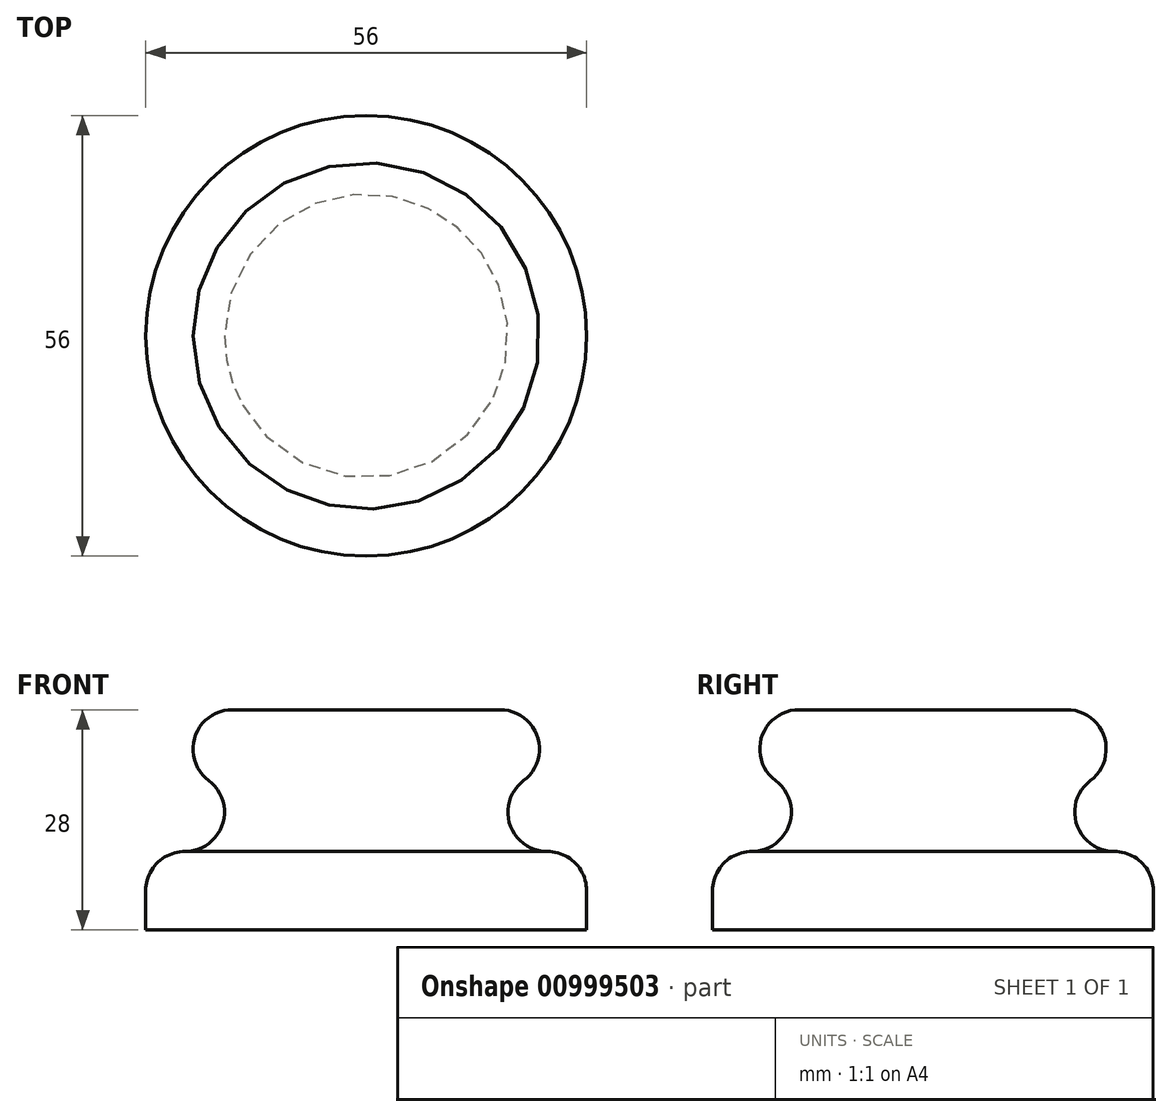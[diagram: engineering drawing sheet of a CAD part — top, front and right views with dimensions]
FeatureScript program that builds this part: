
annotation { "Feature Type Name" : "Feature", "Feature Type Description" : "" }
export const myFeature = defineFeature(function(context is Context, id is Id, definition is map)
    precondition{}
    {
        {
            var Q0;
            Q0=qCreatedBy(makeId("Front.planeOp"),FACE);
            var sketch = newSketch(context, id + "F0", { "sketchPlane" : qUnion([Q0])});
            skLineSegment(sketch, "E0", {"start": v(0, 0) * mm, "end": v(0, 28) * mm});
            skLineSegment(sketch, "E1", {"start": v(0, 0) * mm, "end": v(28, 0) * mm});
            skLineSegment(sketch, "E2", {"start": v(28, 0) * mm, "end": v(28, 5) * mm});
            skLineSegment(sketch, "E3", {"start": v(17, 28) * mm, "end": v(0, 28) * mm});
            skArc(sketch, "E4.filletArc", {"start": v(20, 19) * mm, "mid": v(21.74, 24.58) * mm, "end": v(17, 28) * mm});
            skArc(sketch, "E5.filletArc", {"start": v(20, 19) * mm, "mid": v(18.26, 13.42) * mm, "end": v(23, 10) * mm});
            skArc(sketch, "E6.filletArc", {"start": v(28, 5) * mm, "mid": v(26.54, 8.54) * mm, "end": v(23, 10) * mm});
            skLineSegment(sketch, "E7", {"start": v(7.48, 10) * mm, "end": v(42.98, 10) * mm, "construction": true});
            skSolve(sketch);
        }
        {
            var Q0;
            Q0 = qSketchRegion(id + "F0", true);
            var Q1;
            Q1=sQuery(id+"F0.wireOp",EDGE,"E0");
            revolve(context, id + "F1", {"surfaceOperationType" : NewSurfaceOperationType.NEW, "entities" : qUnion([Q0]), "axis" : qUnion([Q1]), "revolveType" : RevolveType.FULL});
        }
    });
